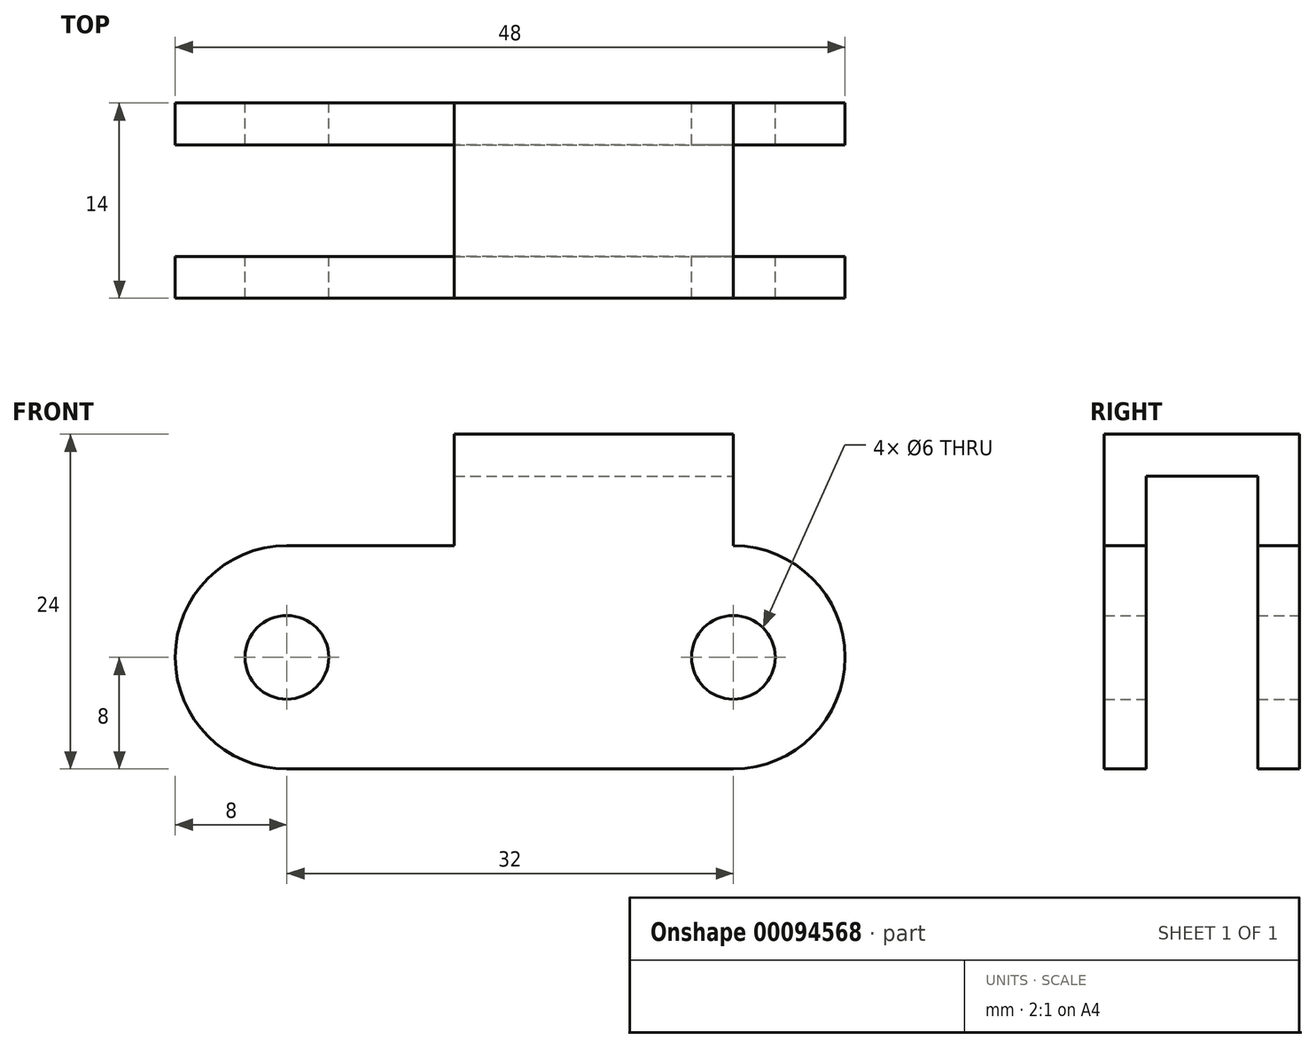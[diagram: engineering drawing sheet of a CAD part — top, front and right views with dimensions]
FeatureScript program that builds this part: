
annotation { "Feature Type Name" : "Feature", "Feature Type Description" : "" }
export const myFeature = defineFeature(function(context is Context, id is Id, definition is map)
    precondition{}
    {
        {
            var Q0;
            Q0=qCreatedBy(makeId("Front.planeOp"),FACE);
            var sketch = newSketch(context, id + "F0", { "sketchPlane" : qUnion([Q0])});
            skLineSegment(sketch, "E0", {"start": v(0, 0) * mm, "end": v(-32, 0) * mm, "construction": true});
            skArc(sketch, "E1.0.startCap", {"start": v(0, 8) * mm, "mid": v(8, 0) * mm, "end": v(0, -8) * mm});
            skArc(sketch, "E1.0.endCap", {"start": v(-32, -8) * mm, "mid": v(-40, 0) * mm, "end": v(-32, 8) * mm});
            skLineSegment(sketch, "E1.0.left", {"start": v(0, -8) * mm, "end": v(-32, -8) * mm});
            skLineSegment(sketch, "E1.0.right", {"start": v(0, 8) * mm, "end": v(-32, 8) * mm});
            skCircle(sketch, "E2", {"center": v(-32, 0) * mm, "radius": 3 * mm});
            skCircle(sketch, "E3.1.0.0", {"center": v(0, 0) * mm, "radius": 3 * mm});
            skLineSegment(sketch, "E3.direction1", {"start": v(-32, 0) * mm, "end": v(0, 0) * mm, "construction": true});
            skLineSegment(sketch, "E4.bottom", {"start": v(0, 8) * mm, "end": v(-20, 8) * mm});
            skLineSegment(sketch, "E4.top", {"start": v(0, 16) * mm, "end": v(-20, 16) * mm});
            skLineSegment(sketch, "E4.left", {"start": v(0, 8) * mm, "end": v(0, 16) * mm});
            skLineSegment(sketch, "E4.right", {"start": v(-20, 8) * mm, "end": v(-20, 16) * mm});
            skSolve(sketch);
        }
        {
            var Q0;
            Q0 = qSketchRegion(id + "F0", true);
            extrude(context, id + "F1", {"entities" : qUnion([Q0]), "endBound" : BoundingType.SYMMETRIC, "depth" : 14 * mm});
        }
        {
            var Q0;
            Q0=qCreatedBy(makeId("Right.planeOp"),FACE);
            var sketch = newSketch(context, id + "F2", { "sketchPlane" : qUnion([Q0])});
            skLineSegment(sketch, "E5.bottom", {"start": v(-4, 13) * mm, "end": v(4, 13) * mm});
            skLineSegment(sketch, "E5.top", {"start": v(-4, -13) * mm, "end": v(4, -13) * mm});
            skLineSegment(sketch, "E5.left", {"start": v(-4, 13) * mm, "end": v(-4, -13) * mm});
            skLineSegment(sketch, "E5.right", {"start": v(4, 13) * mm, "end": v(4, -13) * mm});
            skPoint(sketch, "E5.middle", {"position": v(0, 0) * mm});
            skSolve(sketch);
        }
        {
            var Q0;
            Q0 = qSketchRegion(id + "F2", true);
            extrude(context, id + "F3", {"entities" : qUnion([Q0]), "operationType" : NewBodyOperationType.REMOVE, "endBound" : BoundingType.SYMMETRIC, "oppositeDirection" : true, "depth" : 92.3 * mm});
        }
    });
